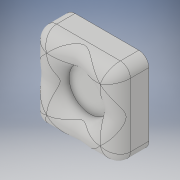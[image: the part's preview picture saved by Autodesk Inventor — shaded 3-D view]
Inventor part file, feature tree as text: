
AUTODESK INVENTOR PART (.ipt)
format: ipt  version: 2019 (Build 230136000, 136)  size: 254,976 bytes
history: native  units: mm
features: fillet x4, extrude x2, sketch x2
ambient origin geometry x8: Origin, YZ Plane, XZ Plane, XY Plane, X Axis, Y Axis, Z Axis, Center Point
bodies: Solid1 (feature_tree)
feature tree (8):
  extrude  "Extrusion1"  Depth=0.5mm
  extrude  "Extrusion2"  Depth=0.06mm
  fillet  "Fillet1"  Radius=0.1mm
  fillet  "Fillet2"  Radius=0.1mm
  fillet  "Fillet3"  Radius=0.09mm
  fillet  "Fillet4"  Radius=0.06mm
  sketch  "Sketch1"  dims[d0=0.5mm d1=0.5mm]
  sketch  "Sketch2"  dims[d2=0.2mm d3=0.0mm d4=0.25mm d5=0.1mm d6=0.0mm d7=0.1mm d8=0.09mm d15=0.06mm d16=0.06mm]
